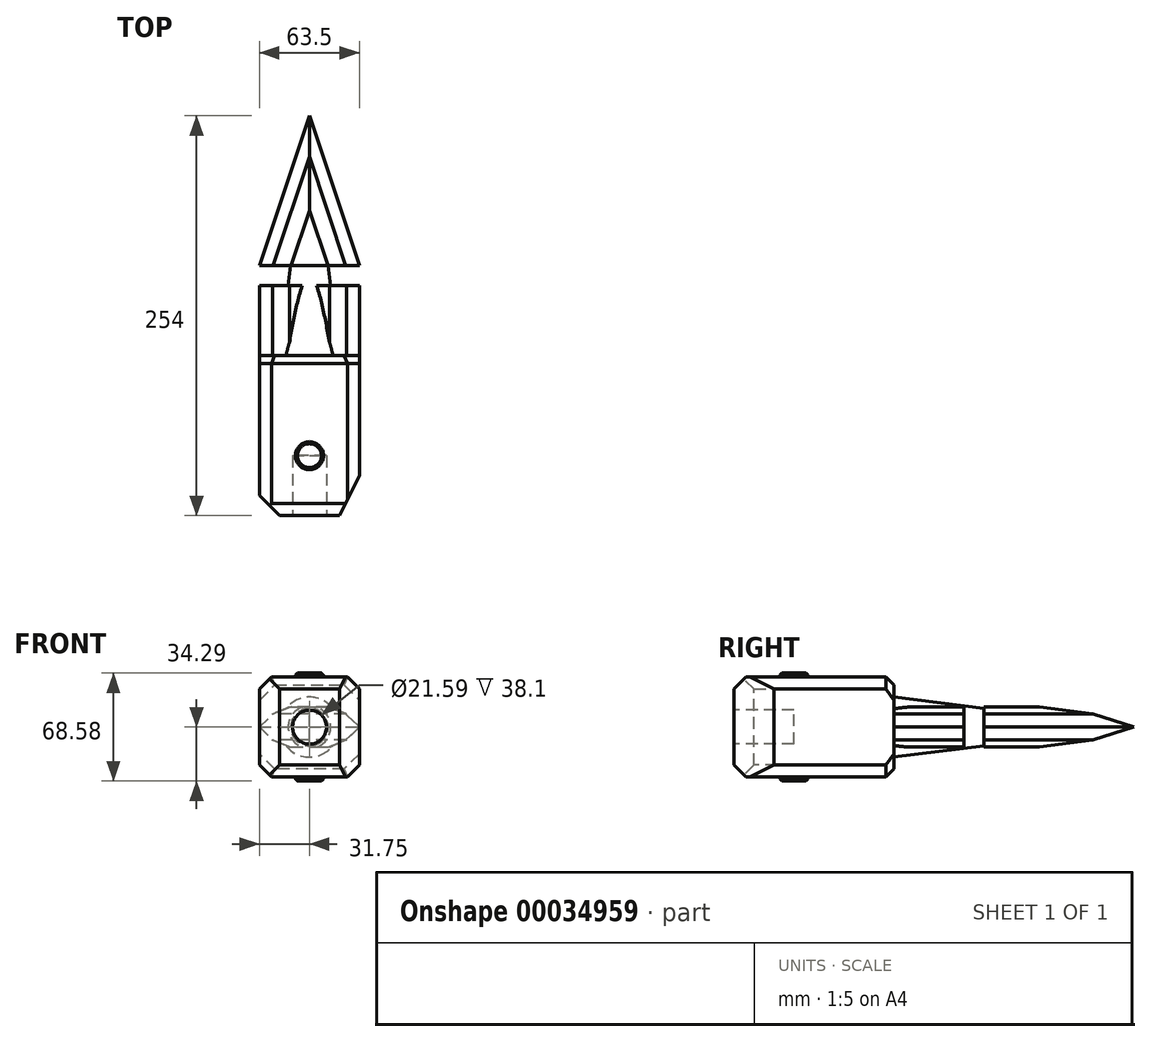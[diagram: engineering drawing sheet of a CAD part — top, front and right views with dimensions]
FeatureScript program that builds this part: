
annotation { "Feature Type Name" : "Feature", "Feature Type Description" : "" }
export const myFeature = defineFeature(function(context is Context, id is Id, definition is map)
    precondition{}
    {
        {
            var Q0;
            Q0=qCreatedBy(makeId("Top.planeOp"),FACE);
            var sketch = newSketch(context, id + "F0", { "sketchPlane" : qUnion([Q0])});
            skLineSegment(sketch, "E0.bottom", {"start": v(-31.75, -50.8) * mm, "end": v(31.75, -50.8) * mm});
            skLineSegment(sketch, "E0.top", {"start": v(-31.75, 50.8) * mm, "end": v(31.75, 50.8) * mm});
            skLineSegment(sketch, "E0.left", {"start": v(-31.75, -50.8) * mm, "end": v(-31.75, 50.8) * mm});
            skLineSegment(sketch, "E0.right", {"start": v(31.75, -50.8) * mm, "end": v(31.75, 50.8) * mm});
            skSolve(sketch);
        }
        {
            var Q0;
            Q0=makeQuery(id+"F0.imprint","IMPRINT",FACE,{"disambiguationData":[TD([[makeQuery(id+"F0.imprint","IMPRINT",EDGE,{"derivedFrom":sQuery(id+"F0.wireOp",EDGE,"E0.bottom")}),1.0]])]});
            extrude(context, id + "F1", {"entities" : qUnion([Q0]), "depth" : 63.5 * mm});
        }
        {
            var Q0;
            Q0=makeQuery(id+"F1.opExtrude","SWEPT_FACE",FACE,{"disambiguationData":[OSD([sQuery(id+"F0.wireOp",EDGE,"E0.bottom")])]});
            var sketch = newSketch(context, id + "F2", { "sketchPlane" : qUnion([Q0])});
            skLineSegment(sketch, "E1", {"start": v(0, 0) * mm, "end": v(0, 63.5) * mm, "construction": true});
            skLineSegment(sketch, "E2", {"start": v(-31.75, 31.75) * mm, "end": v(31.75, 31.75) * mm, "construction": true});
            skCircle(sketch, "E3", {"center": v(0, 31.75) * mm, "radius": 10.8 * mm});
            skSolve(sketch);
        }
        {
            var Q0;
            Q0=makeQuery(id+"F2.imprint","IMPRINT",FACE,{"disambiguationData":[TD([[makeQuery(id+"F2.imprint","IMPRINT",EDGE,{"derivedFrom":sQuery(id+"F2.wireOp",EDGE,"E3")}),1.0]])]});
            extrude(context, id + "F3", {"entities" : qUnion([Q0]), "operationType" : NewBodyOperationType.REMOVE, "oppositeDirection" : true, "depth" : 38.1 * mm});
        }
        {
            var Q0;
            Q0=makeQuery(id+"F1.opExtrude","CAP_FACE",FACE,{"disambiguationData":[OSD([sQuery(id+"F0.wireOp",EDGE,"E0.bottom"),sQuery(id+"F0.wireOp",EDGE,"E0.top"),sQuery(id+"F0.wireOp",EDGE,"E0.left"),sQuery(id+"F0.wireOp",EDGE,"E0.right")])],"isStart":false});
            var sketch = newSketch(context, id + "F4", { "sketchPlane" : qUnion([Q0])});
            skLineSegment(sketch, "E4.bottom", {"start": v(-31.75, -50.8) * mm, "end": v(-19.05, -50.8) * mm});
            skLineSegment(sketch, "E4.top", {"start": v(-31.75, -38.1) * mm, "end": v(-19.05, -38.1) * mm});
            skLineSegment(sketch, "E4.left", {"start": v(-31.75, -50.8) * mm, "end": v(-31.75, -38.1) * mm});
            skLineSegment(sketch, "E4.right", {"start": v(-19.05, -50.8) * mm, "end": v(-19.05, -38.1) * mm});
            skLineSegment(sketch, "E5.bottom", {"start": v(31.75, -50.8) * mm, "end": v(19.05, -50.8) * mm});
            skLineSegment(sketch, "E5.top", {"start": v(31.75, -25.4) * mm, "end": v(19.05, -25.4) * mm});
            skLineSegment(sketch, "E5.left", {"start": v(31.75, -50.8) * mm, "end": v(31.75, -25.4) * mm});
            skLineSegment(sketch, "E5.right", {"start": v(19.05, -50.8) * mm, "end": v(19.05, -25.4) * mm});
            skLineSegment(sketch, "E6", {"start": v(-31.75, -38.1) * mm, "end": v(-19.05, -50.8) * mm});
            skLineSegment(sketch, "E7", {"start": v(19.05, -50.8) * mm, "end": v(31.75, -25.4) * mm});
            skSolve(sketch);
        }
        {
            var Q0;
            Q0=makeQuery(id+"F4.imprint","IMPRINT",FACE,{"disambiguationData":[TD([[makeQuery(id+"F4.imprint","IMPRINT",EDGE,{"derivedFrom":sQuery(id+"F4.wireOp",EDGE,"E4.bottom")}),1.0]])]});
            var Q1;
            Q1=makeQuery(id+"F4.imprint","IMPRINT",FACE,{"disambiguationData":[TD([[makeQuery(id+"F4.imprint","IMPRINT",EDGE,{"derivedFrom":sQuery(id+"F4.wireOp",EDGE,"E5.bottom")}),1.0]])]});
            extrude(context, id + "F5", {"entities" : qUnion([Q0, Q1]), "operationType" : NewBodyOperationType.REMOVE, "oppositeDirection" : true, "depth" : 63.5 * mm});
        }
        {
            var Q0;
            Q0=makeQuery(id+"F1.opExtrude","CAP_EDGE",EDGE,{"disambiguationData":[OSD([sQuery(id+"F0.wireOp",EDGE,"E0.left")])],"isStart":false});
            var Q1;
            Q1=makeQuery(id+"F5.boolean.opBoolean","COPY",EDGE,{"derivedFrom":makeQuery(id+"F5.opExtrude","CAP_EDGE",EDGE,{"disambiguationData":[OSD([sQuery(id+"F4.wireOp",EDGE,"E6")])],"isStart":true})});
            var Q2;
            Q2=makeQuery(id+"F1.opExtrude","CAP_EDGE",EDGE,{"disambiguationData":[OSD([sQuery(id+"F0.wireOp",EDGE,"E0.bottom")])],"isStart":false});
            var Q3;
            Q3=makeQuery(id+"F5.boolean.opBoolean","COPY",EDGE,{"derivedFrom":makeQuery(id+"F5.opExtrude","CAP_EDGE",EDGE,{"disambiguationData":[OSD([sQuery(id+"F4.wireOp",EDGE,"E7")])],"isStart":true})});
            var Q4;
            Q4=makeQuery(id+"F1.opExtrude","CAP_EDGE",EDGE,{"disambiguationData":[OSD([sQuery(id+"F0.wireOp",EDGE,"E0.right")])],"isStart":false});
            var Q5;
            Q5=makeQuery(id+"F5.boolean.opBoolean","COPY",EDGE,{"derivedFrom":makeQuery(id+"F5.opExtrude","CAP_EDGE",EDGE,{"disambiguationData":[OSD([sQuery(id+"F4.wireOp",EDGE,"E7")])],"isStart":false})});
            var Q6;
            Q6=makeQuery(id+"F1.opExtrude","CAP_EDGE",EDGE,{"disambiguationData":[OSD([sQuery(id+"F0.wireOp",EDGE,"E0.right")])],"isStart":true});
            var Q7;
            Q7=makeQuery(id+"F1.opExtrude","CAP_EDGE",EDGE,{"disambiguationData":[OSD([sQuery(id+"F0.wireOp",EDGE,"E0.bottom")])],"isStart":true});
            var Q8;
            Q8=makeQuery(id+"F5.boolean.opBoolean","COPY",EDGE,{"derivedFrom":makeQuery(id+"F5.opExtrude","CAP_EDGE",EDGE,{"disambiguationData":[OSD([sQuery(id+"F4.wireOp",EDGE,"E6")])],"isStart":false})});
            var Q9;
            Q9=makeQuery(id+"F1.opExtrude","CAP_EDGE",EDGE,{"disambiguationData":[OSD([sQuery(id+"F0.wireOp",EDGE,"E0.left")])],"isStart":true});
            chamfer(context, id + "F6", {"entities" : qUnion([Q0, Q1, Q2, Q3, Q4, Q5, Q6, Q7, Q8, Q9]), "width" : 7.62 * mm, "tangentPropagation" : true});
        }
        {
            var Q0;
            Q0=makeQuery(id+"F1.opExtrude","CAP_FACE",FACE,{"disambiguationData":[OSD([sQuery(id+"F0.wireOp",EDGE,"E0.bottom"),sQuery(id+"F0.wireOp",EDGE,"E0.top"),sQuery(id+"F0.wireOp",EDGE,"E0.left"),sQuery(id+"F0.wireOp",EDGE,"E0.right")])],"isStart":false});
            var sketch = newSketch(context, id + "F7", { "sketchPlane" : qUnion([Q0])});
            skCircle(sketch, "E8", {"center": v(0, -12.7) * mm, "radius": 8.9 * mm});
            skSolve(sketch);
        }
        {
            var Q0;
            Q0=makeQuery(id+"F7.imprint","IMPRINT",FACE,{"disambiguationData":[TD([[makeQuery(id+"F7.imprint","IMPRINT",EDGE,{"derivedFrom":sQuery(id+"F7.wireOp",EDGE,"E8")}),1.0]])]});
            extrude(context, id + "F8", {"entities" : qUnion([Q0]), "operationType" : NewBodyOperationType.ADD, "depth" : 2.54 * mm});
        }
        {
            var Q0;
            Q0=makeQuery(id+"F8.opExtrude","CAP_EDGE",EDGE,{"disambiguationData":[OSD([sQuery(id+"F7.wireOp",EDGE,"E8")])],"isStart":false});
            chamfer(context, id + "F9", {"entities" : qUnion([Q0]), "width" : 1.27 * mm, "tangentPropagation" : true});
        }
        {
            var Q0;
            Q0=makeQuery(id+"F1.opExtrude","CAP_FACE",FACE,{"disambiguationData":[OSD([sQuery(id+"F0.wireOp",EDGE,"E0.bottom"),sQuery(id+"F0.wireOp",EDGE,"E0.top"),sQuery(id+"F0.wireOp",EDGE,"E0.left"),sQuery(id+"F0.wireOp",EDGE,"E0.right")])],"isStart":true});
            var sketch = newSketch(context, id + "F10", { "sketchPlane" : qUnion([Q0])});
            skCircle(sketch, "E9", {"center": v(0, 12.7) * mm, "radius": 8.9 * mm});
            skSolve(sketch);
        }
        {
            var Q0;
            Q0=makeQuery(id+"F10.imprint","IMPRINT",FACE,{"disambiguationData":[TD([[makeQuery(id+"F10.imprint","IMPRINT",EDGE,{"derivedFrom":sQuery(id+"F10.wireOp",EDGE,"E9")}),1.0]])]});
            extrude(context, id + "F11", {"entities" : qUnion([Q0]), "operationType" : NewBodyOperationType.ADD, "depth" : 2.54 * mm});
        }
        {
            var Q0;
            Q0=makeQuery(id+"F11.opExtrude","CAP_EDGE",EDGE,{"disambiguationData":[OSD([sQuery(id+"F10.wireOp",EDGE,"E9")])],"isStart":false});
            chamfer(context, id + "F12", {"entities" : qUnion([Q0]), "width" : 1.27 * mm, "tangentPropagation" : true});
        }
        {
            var Q0;
            Q0=qCreatedBy(makeId("Top.planeOp"),FACE);
            cPlane(context, id + "F13", {"entities" : qUnion([Q0]), "cplaneType" : CPlaneType.OFFSET, "offset" : 31.75 * mm, "width" : 152.4 * mm, "height" : 152.4 * mm});
        }
        {
            var Q0;
            Q0=qCreatedBy(id+"F13.planeOp",FACE);
            var sketch = newSketch(context, id + "F14", { "sketchPlane" : qUnion([Q0])});
            skLineSegment(sketch, "E10.0", {"start": v(-24.13, 50.8) * mm, "end": v(24.13, 50.8) * mm});
            skLineSegment(sketch, "E11", {"start": v(0, 50.8) * mm, "end": v(0, 203.2) * mm});
            skLineSegment(sketch, "E12", {"start": v(19.05, 50.8) * mm, "end": v(0, 203.2) * mm});
            skSolve(sketch);
        }
        {
            var Q0;
            {var subQ1=sQuery(id+"F14.wireOp",EDGE,"E11");Q0=makeQuery(id+"F14.imprint","IMPRINT",FACE,{"disambiguationData":[TD([[makeQuery(id+"F14.imprint","IMPRINT",EDGE,{"derivedFrom":subQ1}),-1.0]])]});}
            var Q1;
            Q1=sQuery(id+"F14.wireOp",EDGE,"E11");
            revolve(context, id + "F15", {"operationType" : NewBodyOperationType.ADD, "entities" : qUnion([Q0]), "axis" : qUnion([Q1]), "revolveType" : RevolveType.FULL});
        }
        {
            var Q0;
            Q0=qCreatedBy(id+"F13.planeOp",FACE);
            var sketch = newSketch(context, id + "F16", { "sketchPlane" : qUnion([Q0])});
            skLineSegment(sketch, "E13.0", {"start": v(-24.13, 50.8) * mm, "end": v(24.13, 50.8) * mm});
            skLineSegment(sketch, "E14.0", {"start": v(24.13, 50.8) * mm, "end": v(31.75, 50.8) * mm});
            skLineSegment(sketch, "E15.0", {"start": v(-31.75, 50.8) * mm, "end": v(-24.13, 50.8) * mm});
            skLineSegment(sketch, "E16.bottom", {"start": v(-31.75, 50.8) * mm, "end": v(31.75, 50.8) * mm});
            skLineSegment(sketch, "E16.top", {"start": v(-31.75, 203.2) * mm, "end": v(31.75, 203.2) * mm});
            skLineSegment(sketch, "E16.left", {"start": v(-31.75, 50.8) * mm, "end": v(-31.75, 203.2) * mm});
            skLineSegment(sketch, "E16.right", {"start": v(31.75, 50.8) * mm, "end": v(31.75, 203.2) * mm});
            skLineSegment(sketch, "E17.bottom", {"start": v(-31.75, 95.25) * mm, "end": v(31.75, 95.25) * mm});
            skLineSegment(sketch, "E17.top", {"start": v(-31.75, 107.95) * mm, "end": v(31.75, 107.95) * mm});
            skLineSegment(sketch, "E17.left", {"start": v(-31.75, 95.25) * mm, "end": v(-31.75, 107.95) * mm});
            skLineSegment(sketch, "E17.right", {"start": v(31.75, 95.25) * mm, "end": v(31.75, 107.95) * mm});
            skLineSegment(sketch, "E18", {"start": v(-31.75, 107.95) * mm, "end": v(0, 203.2) * mm});
            skLineSegment(sketch, "E19", {"start": v(0, 203.2) * mm, "end": v(31.75, 107.95) * mm});
            skSolve(sketch);
        }
        {
            var Q0;
            {var subQ0=sQuery(id+"F16.wireOp",EDGE,"E17.bottom");Q0=makeQuery(id+"F16.imprint","IMPRINT",FACE,{"disambiguationData":[TD([[makeQuery(id+"F16.imprint","IMPRINT",EDGE,{"derivedFrom":subQ0}),-1.0]])]});}
            var Q1;
            Q1=makeQuery(id+"F16.imprint","IMPRINT",FACE,{"disambiguationData":[TD([[makeQuery(id+"F16.imprint","IMPRINT",EDGE,{"derivedFrom":sQuery(id+"F16.wireOp",EDGE,"E17.top")}),1.0]])]});
            extrude(context, id + "F17", {"entities" : qUnion([Q0, Q1]), "operationType" : NewBodyOperationType.ADD, "endBound" : BoundingType.SYMMETRIC, "depth" : 25.4 * mm});
        }
        {
            var Q0;
            Q0=makeQuery(id+"F17.opExtrude","CAP_EDGE",EDGE,{"disambiguationData":[OSD([sQuery(id+"F16.wireOp",EDGE,"E19")])],"isStart":false});
            var Q1;
            Q1=makeQuery(id+"F17.opExtrude","CAP_EDGE",EDGE,{"disambiguationData":[OSD([sQuery(id+"F16.wireOp",EDGE,"E18")])],"isStart":false});
            var Q2;
            Q2=makeQuery(id+"F17.opExtrude","CAP_EDGE",EDGE,{"disambiguationData":[OSD([sQuery(id+"F16.wireOp",EDGE,"E19")])],"isStart":true});
            var Q3;
            Q3=makeQuery(id+"F17.opExtrude","CAP_EDGE",EDGE,{"disambiguationData":[OSD([sQuery(id+"F16.wireOp",EDGE,"E18")])],"isStart":true});
            var Q4;
            Q4=makeQuery(id+"F17.opExtrude","CAP_EDGE",EDGE,{"disambiguationData":[OSD([sQuery(id+"F16.wireOp",EDGE,"E16.left")])],"isStart":true});
            var Q5;
            Q5=makeQuery(id+"F17.opExtrude","CAP_EDGE",EDGE,{"disambiguationData":[OSD([sQuery(id+"F16.wireOp",EDGE,"E16.left")])],"isStart":false});
            var Q6;
            Q6=makeQuery(id+"F17.opExtrude","CAP_EDGE",EDGE,{"disambiguationData":[OSD([sQuery(id+"F16.wireOp",EDGE,"E16.right")])],"isStart":false});
            var Q7;
            Q7=makeQuery(id+"F17.opExtrude","CAP_EDGE",EDGE,{"disambiguationData":[OSD([sQuery(id+"F16.wireOp",EDGE,"E16.right")])],"isStart":true});
            chamfer(context, id + "F18", {"entities" : qUnion([Q0, Q1, Q2, Q3, Q4, Q5, Q6, Q7]), "width" : 12.7 * mm, "tangentPropagation" : true});
        }
        {
            var Q0;
            {var subQ0=sQuery(id+"F16.wireOp",EDGE,"E18");Q0=makeQuery(id+"F18.opChamfer","BLEND_EDGE",EDGE,{"blendedFrom":[makeQuery(id+"F17.opExtrude","CAP_EDGE",EDGE,{"disambiguationData":[OSD([subQ0])],"isStart":true}),makeQuery(id+"F17.opExtrude","CAP_FACE",FACE,{"disambiguationData":[OSD([sQuery(id+"F16.wireOp",EDGE,"E17.top"),subQ0,sQuery(id+"F16.wireOp",EDGE,"E19")])],"isStart":true})],"blendedInto":[makeQuery(id+"F17.opExtrude","CAP_FACE",FACE,{"disambiguationData":[OSD([sQuery(id+"F16.wireOp",EDGE,"E17.top"),subQ0,sQuery(id+"F16.wireOp",EDGE,"E19")])],"isStart":true})]});}
            var Q1;
            {var subQ0=sQuery(id+"F16.wireOp",EDGE,"E19");Q1=makeQuery(id+"F18.opChamfer","BLEND_EDGE",EDGE,{"blendedFrom":[makeQuery(id+"F17.opExtrude","CAP_EDGE",EDGE,{"disambiguationData":[OSD([subQ0])],"isStart":true}),makeQuery(id+"F17.opExtrude","CAP_FACE",FACE,{"disambiguationData":[OSD([sQuery(id+"F16.wireOp",EDGE,"E17.top"),sQuery(id+"F16.wireOp",EDGE,"E18"),subQ0])],"isStart":true})],"blendedInto":[makeQuery(id+"F17.opExtrude","CAP_FACE",FACE,{"disambiguationData":[OSD([sQuery(id+"F16.wireOp",EDGE,"E17.top"),sQuery(id+"F16.wireOp",EDGE,"E18"),subQ0])],"isStart":true})]});}
            chamfer(context, id + "F19", {"entities" : qUnion([Q0, Q1]), "width" : 15.24 * mm, "tangentPropagation" : true});
        }
        {
            var Q0;
            {var subQ0=sQuery(id+"F16.wireOp",EDGE,"E19");Q0=makeQuery(id+"F18.opChamfer","BLEND_EDGE",EDGE,{"blendedFrom":[makeQuery(id+"F17.opExtrude","CAP_EDGE",EDGE,{"disambiguationData":[OSD([subQ0])],"isStart":false}),makeQuery(id+"F17.opExtrude","CAP_FACE",FACE,{"disambiguationData":[OSD([sQuery(id+"F16.wireOp",EDGE,"E17.top"),sQuery(id+"F16.wireOp",EDGE,"E18"),subQ0])],"isStart":false})],"blendedInto":[makeQuery(id+"F17.opExtrude","CAP_FACE",FACE,{"disambiguationData":[OSD([sQuery(id+"F16.wireOp",EDGE,"E17.top"),sQuery(id+"F16.wireOp",EDGE,"E18"),subQ0])],"isStart":false})]});}
            var Q1;
            {var subQ0=sQuery(id+"F16.wireOp",EDGE,"E18");Q1=makeQuery(id+"F18.opChamfer","BLEND_EDGE",EDGE,{"blendedFrom":[makeQuery(id+"F17.opExtrude","CAP_EDGE",EDGE,{"disambiguationData":[OSD([subQ0])],"isStart":false}),makeQuery(id+"F17.opExtrude","CAP_FACE",FACE,{"disambiguationData":[OSD([sQuery(id+"F16.wireOp",EDGE,"E17.top"),subQ0,sQuery(id+"F16.wireOp",EDGE,"E19")])],"isStart":false})],"blendedInto":[makeQuery(id+"F17.opExtrude","CAP_FACE",FACE,{"disambiguationData":[OSD([sQuery(id+"F16.wireOp",EDGE,"E17.top"),subQ0,sQuery(id+"F16.wireOp",EDGE,"E19")])],"isStart":false})]});}
            chamfer(context, id + "F20", {"entities" : qUnion([Q0, Q1]), "width" : 15.24 * mm, "tangentPropagation" : true});
        }
        {
            var Q0;
            {var subQ0=sQuery(id+"F16.wireOp",EDGE,"E16.left");var subQ1=sQuery(id+"F16.wireOp",EDGE,"E17.bottom");Q0=makeQuery(id+"F18.opChamfer","BLEND_EDGE",EDGE,{"blendedFrom":[makeQuery(id+"F17.opExtrude","CAP_EDGE",EDGE,{"disambiguationData":[OSD([subQ0])],"isStart":true}),makeQuery(id+"F17.boolean.opBoolean","SPLIT",FACE,{"disambiguationData":[TD([makeQuery(id+"F1.opExtrude","SWEPT_FACE",FACE,{"disambiguationData":[OSD([sQuery(id+"F0.wireOp",EDGE,"E0.left")])]})])],"derivedFrom":makeQuery(id+"F17.opExtrude","CAP_FACE",FACE,{"disambiguationData":[OSD([sQuery(id+"F16.wireOp",EDGE,"E16.bottom"),subQ0,sQuery(id+"F16.wireOp",EDGE,"E16.right"),subQ1])],"isStart":true})})],"blendedInto":[makeQuery(id+"F17.boolean.opBoolean","SPLIT",FACE,{"disambiguationData":[TD([makeQuery(id+"F1.opExtrude","SWEPT_FACE",FACE,{"disambiguationData":[OSD([sQuery(id+"F0.wireOp",EDGE,"E0.left")])]})])],"derivedFrom":makeQuery(id+"F17.opExtrude","CAP_FACE",FACE,{"disambiguationData":[OSD([sQuery(id+"F16.wireOp",EDGE,"E16.bottom"),subQ0,sQuery(id+"F16.wireOp",EDGE,"E16.right"),subQ1])],"isStart":true})})]});}
            var Q1;
            {var subQ0=sQuery(id+"F16.wireOp",EDGE,"E16.left");var subQ1=sQuery(id+"F16.wireOp",EDGE,"E17.bottom");Q1=makeQuery(id+"F18.opChamfer","BLEND_EDGE",EDGE,{"blendedFrom":[makeQuery(id+"F17.opExtrude","CAP_EDGE",EDGE,{"disambiguationData":[OSD([subQ0])],"isStart":false}),makeQuery(id+"F17.boolean.opBoolean","SPLIT",FACE,{"disambiguationData":[TD([makeQuery(id+"F1.opExtrude","SWEPT_FACE",FACE,{"disambiguationData":[OSD([sQuery(id+"F0.wireOp",EDGE,"E0.left")])]})])],"derivedFrom":makeQuery(id+"F17.opExtrude","CAP_FACE",FACE,{"disambiguationData":[OSD([sQuery(id+"F16.wireOp",EDGE,"E16.bottom"),subQ0,sQuery(id+"F16.wireOp",EDGE,"E16.right"),subQ1])],"isStart":false})})],"blendedInto":[makeQuery(id+"F17.boolean.opBoolean","SPLIT",FACE,{"disambiguationData":[TD([makeQuery(id+"F1.opExtrude","SWEPT_FACE",FACE,{"disambiguationData":[OSD([sQuery(id+"F0.wireOp",EDGE,"E0.left")])]})])],"derivedFrom":makeQuery(id+"F17.opExtrude","CAP_FACE",FACE,{"disambiguationData":[OSD([sQuery(id+"F16.wireOp",EDGE,"E16.bottom"),subQ0,sQuery(id+"F16.wireOp",EDGE,"E16.right"),subQ1])],"isStart":false})})]});}
            var Q2;
            {var subQ0=sQuery(id+"F16.wireOp",EDGE,"E16.right");var subQ1=sQuery(id+"F16.wireOp",EDGE,"E17.bottom");Q2=makeQuery(id+"F18.opChamfer","BLEND_EDGE",EDGE,{"blendedFrom":[makeQuery(id+"F17.opExtrude","CAP_EDGE",EDGE,{"disambiguationData":[OSD([subQ0])],"isStart":true}),makeQuery(id+"F17.boolean.opBoolean","SPLIT",FACE,{"disambiguationData":[TD([makeQuery(id+"F1.opExtrude","SWEPT_FACE",FACE,{"disambiguationData":[OSD([sQuery(id+"F0.wireOp",EDGE,"E0.right")])]})])],"derivedFrom":makeQuery(id+"F17.opExtrude","CAP_FACE",FACE,{"disambiguationData":[OSD([sQuery(id+"F16.wireOp",EDGE,"E16.bottom"),sQuery(id+"F16.wireOp",EDGE,"E16.left"),subQ0,subQ1])],"isStart":true})})],"blendedInto":[makeQuery(id+"F17.boolean.opBoolean","SPLIT",FACE,{"disambiguationData":[TD([makeQuery(id+"F1.opExtrude","SWEPT_FACE",FACE,{"disambiguationData":[OSD([sQuery(id+"F0.wireOp",EDGE,"E0.right")])]})])],"derivedFrom":makeQuery(id+"F17.opExtrude","CAP_FACE",FACE,{"disambiguationData":[OSD([sQuery(id+"F16.wireOp",EDGE,"E16.bottom"),sQuery(id+"F16.wireOp",EDGE,"E16.left"),subQ0,subQ1])],"isStart":true})})]});}
            var Q3;
            {var subQ0=sQuery(id+"F16.wireOp",EDGE,"E16.right");var subQ1=sQuery(id+"F16.wireOp",EDGE,"E17.bottom");Q3=makeQuery(id+"F18.opChamfer","BLEND_EDGE",EDGE,{"blendedFrom":[makeQuery(id+"F17.opExtrude","CAP_EDGE",EDGE,{"disambiguationData":[OSD([subQ0])],"isStart":false}),makeQuery(id+"F17.boolean.opBoolean","SPLIT",FACE,{"disambiguationData":[TD([makeQuery(id+"F1.opExtrude","SWEPT_FACE",FACE,{"disambiguationData":[OSD([sQuery(id+"F0.wireOp",EDGE,"E0.right")])]})])],"derivedFrom":makeQuery(id+"F17.opExtrude","CAP_FACE",FACE,{"disambiguationData":[OSD([sQuery(id+"F16.wireOp",EDGE,"E16.bottom"),sQuery(id+"F16.wireOp",EDGE,"E16.left"),subQ0,subQ1])],"isStart":false})})],"blendedInto":[makeQuery(id+"F17.boolean.opBoolean","SPLIT",FACE,{"disambiguationData":[TD([makeQuery(id+"F1.opExtrude","SWEPT_FACE",FACE,{"disambiguationData":[OSD([sQuery(id+"F0.wireOp",EDGE,"E0.right")])]})])],"derivedFrom":makeQuery(id+"F17.opExtrude","CAP_FACE",FACE,{"disambiguationData":[OSD([sQuery(id+"F16.wireOp",EDGE,"E16.bottom"),sQuery(id+"F16.wireOp",EDGE,"E16.left"),subQ0,subQ1])],"isStart":false})})]});}
            chamfer(context, id + "F21", {"entities" : qUnion([Q0, Q1, Q2, Q3]), "width" : 15.24 * mm, "tangentPropagation" : true});
        }
        {
            var Q0;
            Q0=makeQuery(id+"F1.opExtrude","CAP_EDGE",EDGE,{"disambiguationData":[OSD([sQuery(id+"F0.wireOp",EDGE,"E0.top")])],"isStart":false});
            var Q1;
            Q1=makeQuery(id+"F6.opChamfer","BLEND_EDGE",EDGE,{"blendedFrom":[makeQuery(id+"F1.opExtrude","CAP_EDGE",EDGE,{"disambiguationData":[OSD([sQuery(id+"F0.wireOp",EDGE,"E0.right")])],"isStart":false}),makeQuery(id+"F1.opExtrude","SWEPT_FACE",FACE,{"disambiguationData":[OSD([sQuery(id+"F0.wireOp",EDGE,"E0.top")])]})],"blendedInto":[makeQuery(id+"F1.opExtrude","SWEPT_FACE",FACE,{"disambiguationData":[OSD([sQuery(id+"F0.wireOp",EDGE,"E0.top")])]})]});
            var Q2;
            Q2=makeQuery(id+"F6.opChamfer","BLEND_EDGE",EDGE,{"blendedFrom":[makeQuery(id+"F1.opExtrude","CAP_EDGE",EDGE,{"disambiguationData":[OSD([sQuery(id+"F0.wireOp",EDGE,"E0.left")])],"isStart":false}),makeQuery(id+"F1.opExtrude","SWEPT_FACE",FACE,{"disambiguationData":[OSD([sQuery(id+"F0.wireOp",EDGE,"E0.top")])]})],"blendedInto":[makeQuery(id+"F1.opExtrude","SWEPT_FACE",FACE,{"disambiguationData":[OSD([sQuery(id+"F0.wireOp",EDGE,"E0.top")])]})]});
            var Q3;
            Q3=makeQuery(id+"F6.opChamfer","BLEND_EDGE",EDGE,{"blendedFrom":[makeQuery(id+"F1.opExtrude","CAP_EDGE",EDGE,{"disambiguationData":[OSD([sQuery(id+"F0.wireOp",EDGE,"E0.right")])],"isStart":true}),makeQuery(id+"F1.opExtrude","SWEPT_FACE",FACE,{"disambiguationData":[OSD([sQuery(id+"F0.wireOp",EDGE,"E0.top")])]})],"blendedInto":[makeQuery(id+"F1.opExtrude","SWEPT_FACE",FACE,{"disambiguationData":[OSD([sQuery(id+"F0.wireOp",EDGE,"E0.top")])]})]});
            var Q4;
            Q4=makeQuery(id+"F6.opChamfer","BLEND_EDGE",EDGE,{"blendedFrom":[makeQuery(id+"F1.opExtrude","CAP_EDGE",EDGE,{"disambiguationData":[OSD([sQuery(id+"F0.wireOp",EDGE,"E0.left")])],"isStart":true}),makeQuery(id+"F1.opExtrude","SWEPT_FACE",FACE,{"disambiguationData":[OSD([sQuery(id+"F0.wireOp",EDGE,"E0.top")])]})],"blendedInto":[makeQuery(id+"F1.opExtrude","SWEPT_FACE",FACE,{"disambiguationData":[OSD([sQuery(id+"F0.wireOp",EDGE,"E0.top")])]})]});
            var Q5;
            Q5=makeQuery(id+"F1.opExtrude","CAP_EDGE",EDGE,{"disambiguationData":[OSD([sQuery(id+"F0.wireOp",EDGE,"E0.top")])],"isStart":true});
            chamfer(context, id + "F22", {"entities" : qUnion([Q0, Q1, Q2, Q3, Q4, Q5]), "width" : 5.08 * mm, "tangentPropagation" : true});
        }
    });
